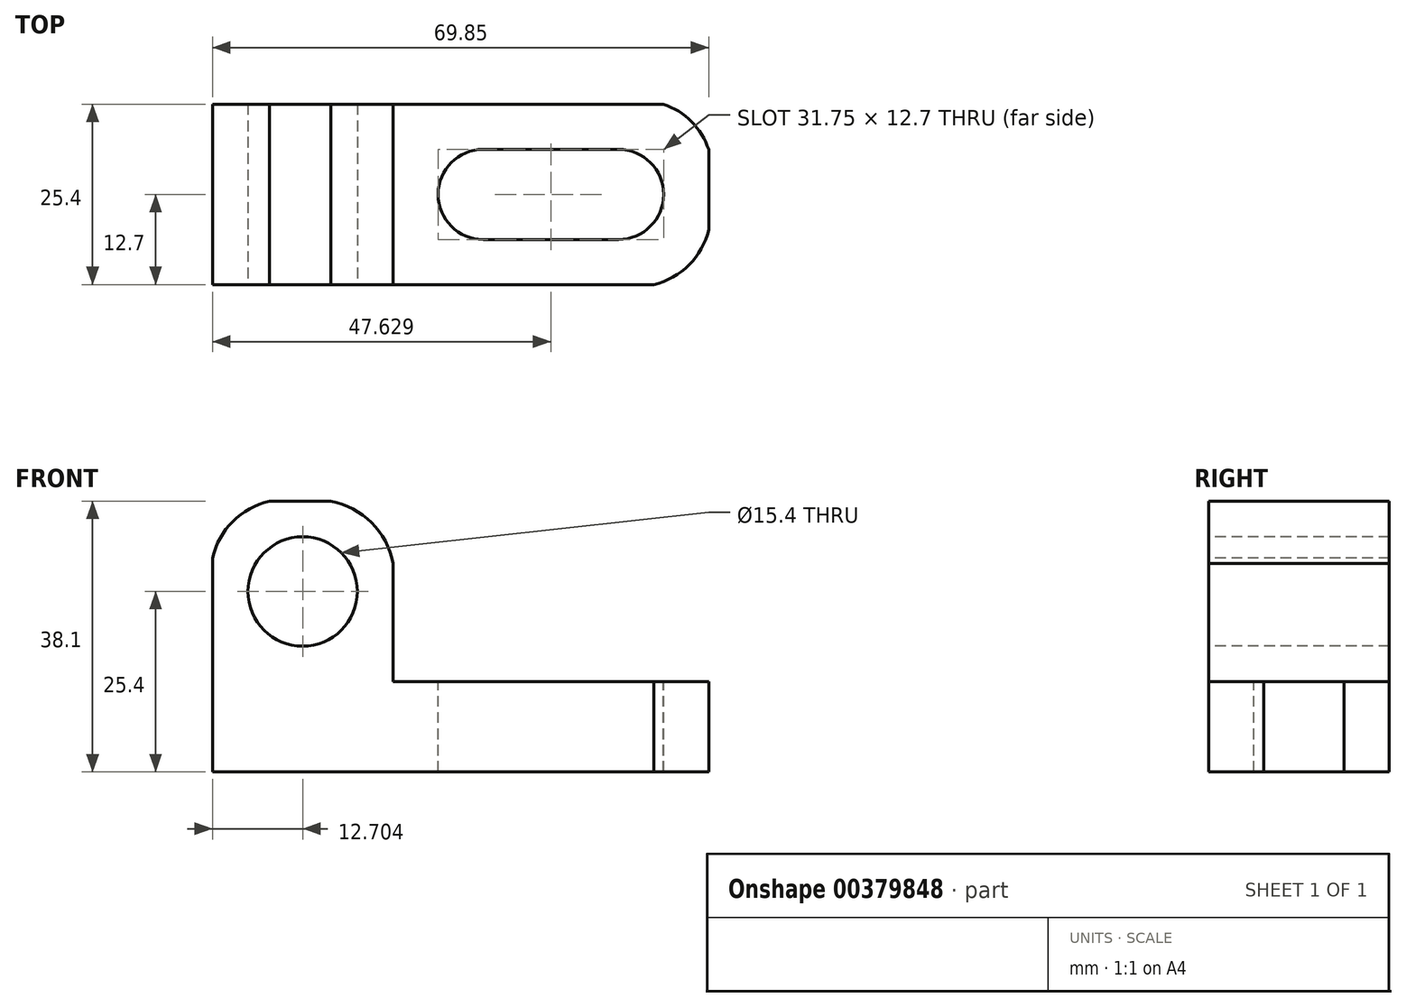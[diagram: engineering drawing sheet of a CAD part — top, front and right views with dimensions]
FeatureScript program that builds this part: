
annotation { "Feature Type Name" : "Feature", "Feature Type Description" : "" }
export const myFeature = defineFeature(function(context is Context, id is Id, definition is map)
    precondition{}
    {
        {
            var Q0;
            Q0=qCreatedBy(makeId("Front.planeOp"),FACE);
            var sketch = newSketch(context, id + "F0", { "sketchPlane" : qUnion([Q0])});
            skLineSegment(sketch, "E0", {"start": v(-37.23, 38.1) * mm, "end": v(-37.23, 0) * mm});
            skLineSegment(sketch, "E1", {"start": v(-37.23, 0) * mm, "end": v(32.62, 0) * mm});
            skLineSegment(sketch, "E2", {"start": v(32.62, 0) * mm, "end": v(32.62, 12.7) * mm});
            skLineSegment(sketch, "E3", {"start": v(-37.23, 38.1) * mm, "end": v(-11.83, 38.1) * mm});
            skLineSegment(sketch, "E4", {"start": v(-11.83, 38.1) * mm, "end": v(-11.83, 12.7) * mm});
            skLineSegment(sketch, "E5", {"start": v(-11.83, 12.7) * mm, "end": v(32.62, 12.7) * mm});
            skSolve(sketch);
        }
        {
            var Q0;
            Q0=makeQuery(id+"F0.imprint","IMPRINT",FACE,{"disambiguationData":[TD([[makeQuery(id+"F0.imprint","IMPRINT",EDGE,{"derivedFrom":sQuery(id+"F0.wireOp",EDGE,"E0")}),1.0]])]});
            extrude(context, id + "F1", {"entities" : qUnion([Q0]), "depth" : 25.4 * mm});
        }
        {
            var Q0;
            Q0=makeQuery(id+"F1.opExtrude","CAP_FACE",FACE,{"disambiguationData":[OSD([sQuery(id+"F0.wireOp",EDGE,"E0"),sQuery(id+"F0.wireOp",EDGE,"E1"),sQuery(id+"F0.wireOp",EDGE,"E2"),sQuery(id+"F0.wireOp",EDGE,"E3"),sQuery(id+"F0.wireOp",EDGE,"E4"),sQuery(id+"F0.wireOp",EDGE,"E5")])],"isStart":false});
            var sketch = newSketch(context, id + "F2", { "sketchPlane" : qUnion([Q0])});
            skCircle(sketch, "E6", {"center": v(-24.53, 25.4) * mm, "radius": 7.7 * mm});
            skSolve(sketch);
        }
        {
            var Q0;
            Q0=makeQuery(id+"F2.imprint","IMPRINT",FACE,{"disambiguationData":[TD([[makeQuery(id+"F2.imprint","IMPRINT",EDGE,{"derivedFrom":sQuery(id+"F2.wireOp",EDGE,"E6")}),1.0]])]});
            extrude(context, id + "F3", {"entities" : qUnion([Q0]), "operationType" : NewBodyOperationType.REMOVE, "oppositeDirection" : true, "depth" : 25.4 * mm});
        }
        {
            var Q0;
            Q0=makeQuery(id+"F1.opExtrude","CAP_FACE",FACE,{"disambiguationData":[OSD([sQuery(id+"F0.wireOp",EDGE,"E0"),sQuery(id+"F0.wireOp",EDGE,"E1"),sQuery(id+"F0.wireOp",EDGE,"E2"),sQuery(id+"F0.wireOp",EDGE,"E3"),sQuery(id+"F0.wireOp",EDGE,"E4"),sQuery(id+"F0.wireOp",EDGE,"E5")])],"isStart":false});
            var sketch = newSketch(context, id + "F4", { "sketchPlane" : qUnion([Q0])});
            skArc(sketch, "E7", {"start": v(-24.53, 38.1) * mm, "mid": v(-34.38, 35.25) * mm, "end": v(-37.23, 25.4) * mm});
            skArc(sketch, "E8", {"start": v(-11.83, 25.4) * mm, "mid": v(-14.84, 35.09) * mm, "end": v(-24.53, 38.1) * mm});
            skSolve(sketch);
        }
        {
            var Q0;
            {var subQ0=sQuery(id+"F4.wireOp",EDGE,"E7");var subQ1=makeQuery(id+"F1.opExtrude","CAP_EDGE",EDGE,{"disambiguationData":[OSD([sQuery(id+"F0.wireOp",EDGE,"E3")])],"isStart":false});var subQ2=makeQuery(id+"F4.imprint","INTERSECT",VERTEX,{"derivedFrom":[subQ1,subQ0]});Q0=makeQuery(id+"F4.imprint","IMPRINT",FACE,{"disambiguationData":[TD([[makeQuery(id+"F4.imprint","IMPRINT",EDGE,{"disambiguationData":[TD([[subQ2,-1.0]])],"derivedFrom":subQ0}),-1.0]])]});}
            var Q1;
            {var subQ0=sQuery(id+"F4.wireOp",EDGE,"E8");var subQ1=makeQuery(id+"F1.opExtrude","CAP_EDGE",EDGE,{"disambiguationData":[OSD([sQuery(id+"F0.wireOp",EDGE,"E4")])],"isStart":false});var subQ2=makeQuery(id+"F4.imprint","INTERSECT",VERTEX,{"disambiguationData":[OD(1.0)],"derivedFrom":[subQ1,subQ0]});Q1=makeQuery(id+"F4.imprint","IMPRINT",FACE,{"disambiguationData":[TD([[makeQuery(id+"F4.imprint","IMPRINT",EDGE,{"disambiguationData":[TD([[subQ2,-1.0]])],"derivedFrom":subQ0}),-1.0]])]});}
            extrude(context, id + "F5", {"entities" : qUnion([Q0, Q1]), "operationType" : NewBodyOperationType.REMOVE, "oppositeDirection" : true, "depth" : 25.4 * mm});
        }
        {
            var Q0;
            Q0=makeQuery(id+"F1.opExtrude","SWEPT_FACE",FACE,{"disambiguationData":[OSD([sQuery(id+"F0.wireOp",EDGE,"E5")])]});
            var sketch = newSketch(context, id + "F6", { "sketchPlane" : qUnion([Q0])});
            skCircle(sketch, "E9", {"center": v(0.87, -12.7) * mm, "radius": 6.35 * mm});
            skCircle(sketch, "E10", {"center": v(19.92, -12.7) * mm, "radius": 6.35 * mm});
            skLineSegment(sketch, "E11", {"start": v(0.87, -19.05) * mm, "end": v(19.92, -19.05) * mm});
            skLineSegment(sketch, "E12", {"start": v(0.87, -6.35) * mm, "end": v(19.92, -6.35) * mm});
            skSolve(sketch);
        }
        {
            var Q0;
            {var subQ0=sQuery(id+"F6.wireOp",EDGE,"E10");var subQ1=makeQuery(id+"F6.imprint","INTERSECT",VERTEX,{"derivedFrom":[subQ0,sQuery(id+"F6.wireOp",EDGE,"E11")]});Q0=makeQuery(id+"F6.imprint","IMPRINT",FACE,{"disambiguationData":[TD([[makeQuery(id+"F6.imprint","IMPRINT",EDGE,{"disambiguationData":[TD([[subQ1,1.0]])],"derivedFrom":subQ0}),1.0]])]});}
            var Q1;
            {var subQ0=sQuery(id+"F6.wireOp",EDGE,"E11");Q1=makeQuery(id+"F6.imprint","IMPRINT",FACE,{"disambiguationData":[TD([[makeQuery(id+"F6.imprint","IMPRINT",EDGE,{"derivedFrom":subQ0}),1.0]])]});}
            var Q2;
            {var subQ0=sQuery(id+"F6.wireOp",EDGE,"E9");var subQ1=makeQuery(id+"F6.imprint","INTERSECT",VERTEX,{"derivedFrom":[subQ0,sQuery(id+"F6.wireOp",EDGE,"E11")]});Q2=makeQuery(id+"F6.imprint","IMPRINT",FACE,{"disambiguationData":[TD([[makeQuery(id+"F6.imprint","IMPRINT",EDGE,{"disambiguationData":[TD([[subQ1,1.0]])],"derivedFrom":subQ0}),1.0]])]});}
            extrude(context, id + "F7", {"entities" : qUnion([Q0, Q1, Q2]), "operationType" : NewBodyOperationType.REMOVE, "oppositeDirection" : true, "depth" : 12.7 * mm});
        }
        {
            var Q0;
            Q0=makeQuery(id+"F1.opExtrude","SWEPT_FACE",FACE,{"disambiguationData":[OSD([sQuery(id+"F0.wireOp",EDGE,"E5")])]});
            var sketch = newSketch(context, id + "F8", { "sketchPlane" : qUnion([Q0])});
            skArc(sketch, "E13", {"start": v(32.62, -12.7) * mm, "mid": v(30.19, -2.44) * mm, "end": v(19.92, 0) * mm});
            skArc(sketch, "E14", {"start": v(19.92, -25.4) * mm, "mid": v(29.85, -22.62) * mm, "end": v(32.62, -12.7) * mm});
            skSolve(sketch);
        }
        {
            var Q0;
            {var subQ0=sQuery(id+"F8.wireOp",EDGE,"E13");var subQ1=sQuery(id+"F0.wireOp",EDGE,"E5");var subQ4=makeQuery(id+"F1.opExtrude","CAP_EDGE",EDGE,{"disambiguationData":[OSD([subQ1])],"isStart":true});var subQ5=makeQuery(id+"F8.imprint","INTERSECT",VERTEX,{"disambiguationData":[OD(1.0)],"derivedFrom":[subQ4,subQ0]});Q0=makeQuery(id+"F8.imprint","IMPRINT",FACE,{"disambiguationData":[TD([[makeQuery(id+"F8.imprint","IMPRINT",EDGE,{"disambiguationData":[TD([[subQ5,1.0]])],"derivedFrom":subQ0}),-1.0]])]});}
            var Q1;
            {var subQ0=sQuery(id+"F8.wireOp",EDGE,"E14");var subQ1=sQuery(id+"F0.wireOp",EDGE,"E5");var subQ2=makeQuery(id+"F1.opExtrude","CAP_EDGE",EDGE,{"disambiguationData":[OSD([subQ1])],"isStart":false});var subQ3=makeQuery(id+"F8.imprint","INTERSECT",VERTEX,{"disambiguationData":[OD(1.0)],"derivedFrom":[subQ2,subQ0]});Q1=makeQuery(id+"F8.imprint","IMPRINT",FACE,{"disambiguationData":[TD([[makeQuery(id+"F8.imprint","IMPRINT",EDGE,{"disambiguationData":[TD([[subQ3,-1.0]])],"derivedFrom":subQ0}),-1.0]])]});}
            extrude(context, id + "F9", {"entities" : qUnion([Q0, Q1]), "operationType" : NewBodyOperationType.REMOVE, "oppositeDirection" : true, "depth" : 12.7 * mm});
        }
    });
